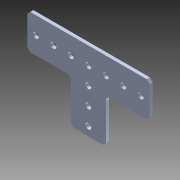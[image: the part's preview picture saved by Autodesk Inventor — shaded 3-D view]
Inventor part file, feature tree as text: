
AUTODESK INVENTOR PART (.ipt)
format: ipt  version: 2014 (Build 180170000, 170)  size: 139,264 bytes
history: native  units: in
note: dims shown in document units (in); Inventor stores cm internally (conversion verified against a paired STEP export)
features: fillet x1, other x1, imported_body x1
ambient origin geometry x8: Origin, YZ Plane, XZ Plane, XY Plane, X Axis, Y Axis, Z Axis, Center Point
bodies: Body1 (feature_tree)
feature tree (3):
  fillet  "Fillet1"  [1 undecoded]
  other  "217-3557-STEP1"
  imported_body  "Base1"
note: 1 required parameter value undecoded (feature->parameter linkage not recoverable at this tier; creation-order binding heuristic only, values carry confidence <= 0.55)
